# Revit family: Sink-Kitchen-All_In_One-KOHLER-Kennon-K-R8437_1
name_source: partatom
category: Plumbing Fixtures
units: mm (PartAtom-declared; Revit-internal decimal feet)

## family parameters
Cut with Voids When Loaded = No
Host = Face
Maintain Annotation Orientation = No
OmniClass Number = 23.31.13.00
OmniClass Title = Sinks
Part Type = Normal
Room Calculation Point = No
Round Connector Dimension = Use Diameter
Shared = No

## types (1)
- CM1-Matte Black
    ADA Compliant = No
    Assembly Code = D2010400
    CW Connection = Yes
    Cold Water Inlet = Cold Water Inlet
    Date Modified = 02/28/2022
    Default Elevation = 36"
    Description = Single-bowl top-mount/undermount kitchen sink kit
    Drain Included = No
    Faucet Height = 15 1/16"
    Finish = Kohler-Neoroc-CM1-Matte_Black
    Flow Rate = 2 GPM
    HW Connection = Yes
    Handle Clearance = 4 3/8"
    Height = 12 3/16"
    Hot Water Inlet = Hot Water Inlet
    Length = 21 15/16"
    Manufacturer = KOHLER Co.
    Master Format 2014 = 22 41 16
    Master Format 2014 Name = Residential Lavatories and Sinks
    Material = Neoroc
    Model = K-R8437-2PC-CM1
    Pressure = 60.00 psi
    Product Documentation Link = https://www.us.kohler.com
    Product Name = Kennon
    Product Page URL = http://www.us.kohler.com
    Secondary Finish = Kohler-Metal-VS-Vibrant_Stainless
    Spout Reach = 8 15/16"
    Type = 1
    URL = https://www.us.kohler.com
    Vent Connection = No
    Waste Connection = Yes
    Waste Water Outlet = Waste Water Outlet
    WaterSense Certified = No
    Width = 33"

## geometry (parser evidence)
native form markers: Sweep x9
no freeform markers — native parametric forms only
